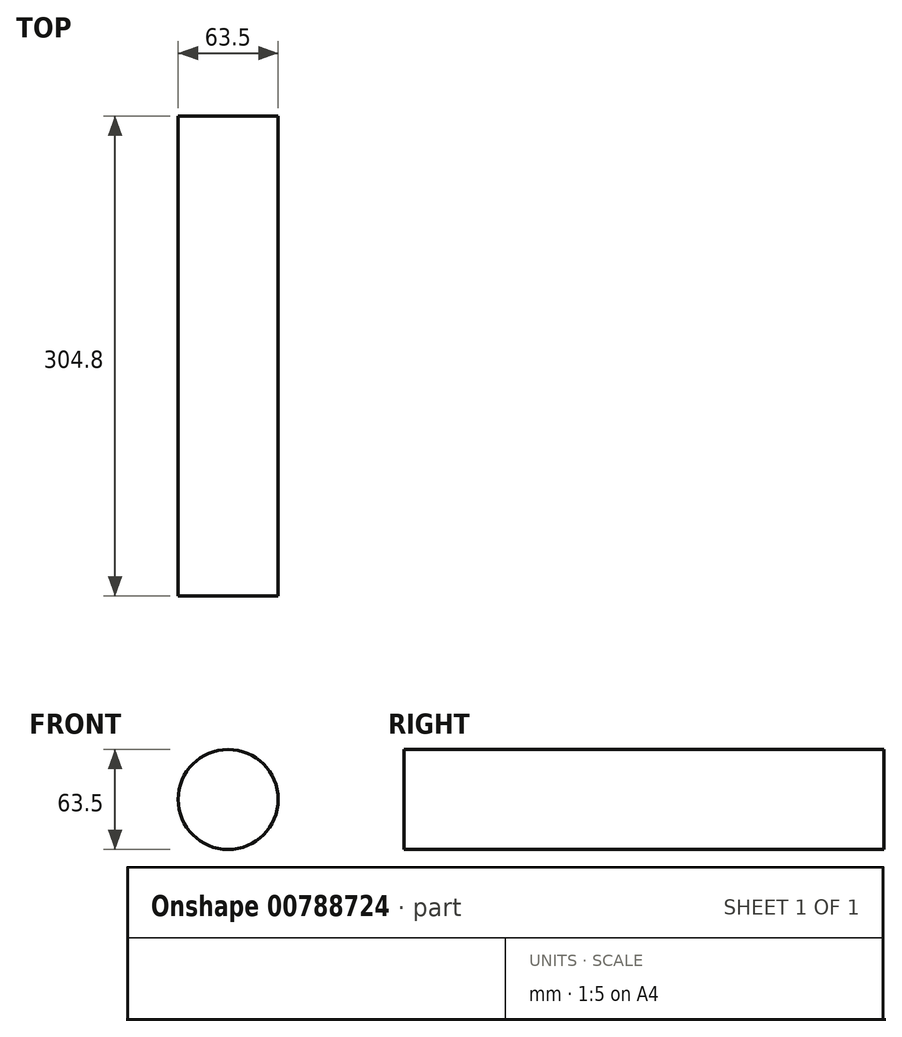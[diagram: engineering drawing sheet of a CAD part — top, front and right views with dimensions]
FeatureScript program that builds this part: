
annotation { "Feature Type Name" : "Feature", "Feature Type Description" : "" }
export const myFeature = defineFeature(function(context is Context, id is Id, definition is map)
    precondition{}
    {
        {
            var Q0;
            Q0=qCreatedBy(makeId("Front.planeOp"),FACE);
            var sketch = newSketch(context, id + "F0", { "sketchPlane" : qUnion([Q0])});
            skCircle(sketch, "E0", {"center": v(0, 0) * mm, "radius": 31.75 * mm});
            skSolve(sketch);
        }
        {
            var Q0;
            Q0 = qSketchRegion(id + "F0", true);
            extrude(context, id + "F1", {"entities" : qUnion([Q0]), "depth" : 304.8 * mm, "offsetDistance" : 25.4 * mm});
        }
    });
